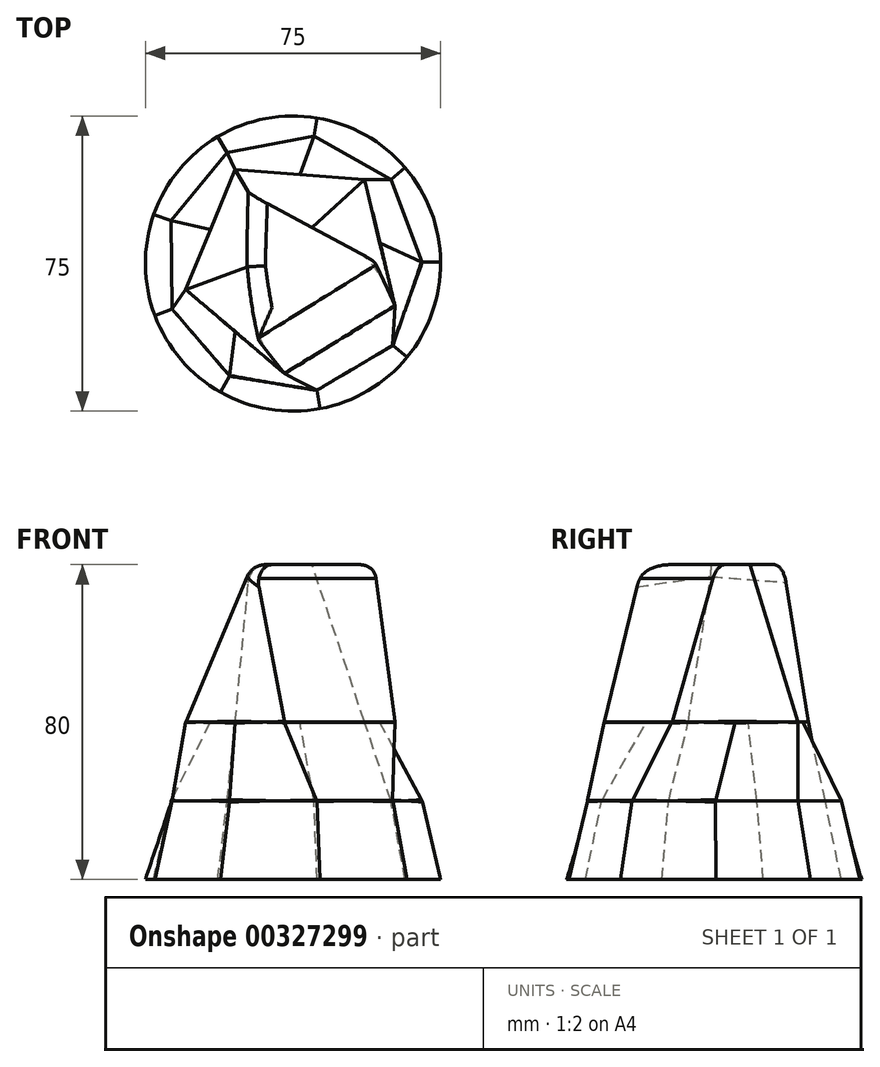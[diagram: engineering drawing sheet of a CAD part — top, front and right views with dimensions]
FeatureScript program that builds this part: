
annotation { "Feature Type Name" : "Feature", "Feature Type Description" : "" }
export const myFeature = defineFeature(function(context is Context, id is Id, definition is map)
    precondition{}
    {
        {
            var Q0;
            Q0=qCreatedBy(makeId("Top.planeOp"),FACE);
            var sketch = newSketch(context, id + "F0", { "sketchPlane" : qUnion([Q0])});
            skCircle(sketch, "E0", {"center": v(0, 0) * mm, "radius": 37.5 * mm});
            skSolve(sketch);
        }
        {
            var Q0;
            Q0=qCreatedBy(makeId("Top.planeOp"),FACE);
            cPlane(context, id + "F1", {"entities" : qUnion([Q0]), "cplaneType" : CPlaneType.OFFSET, "offset" : 20 * mm, "width" : 150 * mm, "height" : 150 * mm});
        }
        {
            var Q0;
            Q0=qCreatedBy(id+"F1.planeOp",FACE);
            var sketch = newSketch(context, id + "F2", { "sketchPlane" : qUnion([Q0])});
            skLineSegment(sketch, "E1.0", {"start": v(-16.7, 28.2) * mm, "end": v(5.34, 32.34) * mm});
            skLineSegment(sketch, "E1.1", {"start": v(5.34, 32.34) * mm, "end": v(24.88, 21.34) * mm});
            skLineSegment(sketch, "E1.2", {"start": v(24.88, 21.34) * mm, "end": v(32.77, 0.35) * mm});
            skLineSegment(sketch, "E1.3", {"start": v(32.77, 0.35) * mm, "end": v(25.33, -20.8) * mm});
            skLineSegment(sketch, "E1.4", {"start": v(25.33, -20.8) * mm, "end": v(6.04, -32.21) * mm});
            skLineSegment(sketch, "E1.5", {"start": v(6.04, -32.21) * mm, "end": v(-16.08, -28.56) * mm});
            skLineSegment(sketch, "E1.6", {"start": v(-16.08, -28.56) * mm, "end": v(-30.68, -11.54) * mm});
            skLineSegment(sketch, "E1.7", {"start": v(-30.68, -11.54) * mm, "end": v(-30.92, 10.88) * mm});
            skLineSegment(sketch, "E1.8", {"start": v(-30.92, 10.88) * mm, "end": v(-16.7, 28.2) * mm});
            skSolve(sketch);
        }
        {
            var Q0;
            Q0=qCreatedBy(id+"F1.planeOp",FACE);
            cPlane(context, id + "F3", {"entities" : qUnion([Q0]), "cplaneType" : CPlaneType.OFFSET, "offset" : 20 * mm, "width" : 150 * mm, "height" : 150 * mm});
        }
        {
            var Q0;
            Q0=qCreatedBy(id+"F3.planeOp",FACE);
            var sketch = newSketch(context, id + "F4", { "sketchPlane" : qUnion([Q0])});
            skLineSegment(sketch, "E2.0", {"start": v(-14.68, 23.89) * mm, "end": v(18.18, 21.34) * mm});
            skLineSegment(sketch, "E2.1", {"start": v(18.18, 21.34) * mm, "end": v(25.92, -10.7) * mm});
            skLineSegment(sketch, "E2.2", {"start": v(25.92, -10.7) * mm, "end": v(-2.17, -27.95) * mm});
            skLineSegment(sketch, "E2.3", {"start": v(-2.17, -27.95) * mm, "end": v(-27.25, -6.58) * mm});
            skLineSegment(sketch, "E2.4", {"start": v(-27.25, -6.58) * mm, "end": v(-14.68, 23.89) * mm});
            skSolve(sketch);
        }
        {
            var Q0;
            Q0=qCreatedBy(id+"F3.planeOp",FACE);
            cPlane(context, id + "F5", {"entities" : qUnion([Q0]), "cplaneType" : CPlaneType.OFFSET, "offset" : 20 * mm, "width" : 150 * mm, "height" : 150 * mm});
        }
        {
            var Q0;
            Q0=qCreatedBy(id+"F5.planeOp",FACE);
            cPlane(context, id + "F6", {"entities" : qUnion([Q0]), "cplaneType" : CPlaneType.OFFSET, "offset" : 20 * mm, "width" : 150 * mm, "height" : 150 * mm});
        }
        {
            var Q0;
            Q0=qCreatedBy(id+"F6.planeOp",FACE);
            var sketch = newSketch(context, id + "F7", { "sketchPlane" : qUnion([Q0])});
            skLineSegment(sketch, "E3.0", {"start": v(-10.94, 17.56) * mm, "end": v(20.67, 0.7) * mm});
            skLineSegment(sketch, "E3.1", {"start": v(20.67, 0.7) * mm, "end": v(-9.74, -18.25) * mm});
            skLineSegment(sketch, "E3.2", {"start": v(-9.74, -18.25) * mm, "end": v(-10.94, 17.56) * mm});
            skSolve(sketch);
        }
        {
            var Q0;
            Q0 = qSketchRegion(id + "F0", true);
            var Q1;
            Q1 = qSketchRegion(id + "F2", true);
            loft(context, id + "F8", {"sheetProfilesArray" : [{ "sheetProfileEntities" : qUnion([Q0]) }, { "sheetProfileEntities" : qUnion([Q1]) }]});
        }
        {
            var Q1;
            Q1 = qSketchRegion(id + "F2", true);
            var Q2;
            Q2 = qSketchRegion(id + "F4", true);
            loft(context, id + "F9", {"operationType" : NewBodyOperationType.ADD, "sheetProfilesArray" : [{ "sheetProfileEntities" : qUnion([Q1]) }, { "sheetProfileEntities" : qUnion([Q2]) }]});
        }
        {
            var Q1;
            Q1 = qSketchRegion(id + "F4", true);
            var Q2;
            Q2 = qSketchRegion(id + "F7", true);
            loft(context, id + "F10", {"operationType" : NewBodyOperationType.ADD, "sheetProfilesArray" : [{ "sheetProfileEntities" : qUnion([Q1]) }, { "sheetProfileEntities" : qUnion([Q2]) }]});
        }
        {
            var Q0;
            {var subQ0=sQuery(id+"F7.wireOp",EDGE,"E3.1");var subQ1=sQuery(id+"F7.wireOp",EDGE,"E3.2");var subQ2=sQuery(id+"F7.wireOp",EDGE,"E3.0");Q0=makeQuery(id+"F10.opLoft","MID_CAP_EDGE",EDGE,{"disambiguationData":[OSD([subQ2,subQ0,subQ1]),TDD([makeQuery(id+"F7.imprint","INTERSECT",VERTEX,{"derivedFrom":[subQ2,subQ0]}),makeQuery(id+"F7.imprint","INTERSECT",VERTEX,{"derivedFrom":[subQ0,subQ1]}),makeQuery(id+"F7.imprint","IMPRINT",EDGE,{"derivedFrom":subQ0})])],"capPos":1.0});}
            var Q1;
            {var subQ0=sQuery(id+"F7.wireOp",EDGE,"E3.0");var subQ1=sQuery(id+"F7.wireOp",EDGE,"E3.1");var subQ2=sQuery(id+"F7.wireOp",EDGE,"E3.2");Q1=makeQuery(id+"F10.opLoft","MID_CAP_EDGE",EDGE,{"disambiguationData":[OSD([subQ0,subQ1,subQ2]),TDD([makeQuery(id+"F7.imprint","INTERSECT",VERTEX,{"derivedFrom":[subQ0,subQ2]}),makeQuery(id+"F7.imprint","INTERSECT",VERTEX,{"derivedFrom":[subQ0,subQ1]}),makeQuery(id+"F7.imprint","IMPRINT",EDGE,{"derivedFrom":subQ0})])],"capPos":1.0});}
            var Q2;
            Q2=makeQuery(id+"F10.opLoft","MID_CAP_EDGE",EDGE,{"disambiguationData":[OSD([sQuery(id+"F4.wireOp",EDGE,"E2.0"),sQuery(id+"F4.wireOp",EDGE,"E2.3"),sQuery(id+"F4.wireOp",EDGE,"E2.4"),sQuery(id+"F7.wireOp",EDGE,"E3.2")])],"capPos":1.0});
            var Q3;
            Q3=makeQuery(id+"F10.opLoft","MID_CAP_EDGE",EDGE,{"disambiguationData":[OSD([sQuery(id+"F4.wireOp",EDGE,"E2.0"),sQuery(id+"F4.wireOp",EDGE,"E2.4"),sQuery(id+"F7.wireOp",EDGE,"E3.0"),sQuery(id+"F7.wireOp",EDGE,"E3.2")])],"capPos":1.0});
            var Q4;
            Q4=makeQuery(id+"F10.opLoft","MID_CAP_EDGE",EDGE,{"disambiguationData":[OSD([sQuery(id+"F4.wireOp",EDGE,"E2.3"),sQuery(id+"F4.wireOp",EDGE,"E2.4"),sQuery(id+"F7.wireOp",EDGE,"E3.1"),sQuery(id+"F7.wireOp",EDGE,"E3.2")])],"capPos":1.0});
            fillet(context, id + "F11", {"entities" : qUnion([Q0, Q1, Q2, Q3, Q4]), "radius" : 5 * mm, "tangentPropagation" : true, "allowEdgeOverflow" : false});
        }
        {
            var Q0;
            {var subQ0=sQuery(id+"F4.wireOp",EDGE,"E2.4");var subQ1=sQuery(id+"F4.wireOp",EDGE,"E2.3");var subQ2=sQuery(id+"F4.wireOp",EDGE,"E2.2");Q0=makeQuery(id+"F10.boolean.opBoolean","MERGE",EDGE,{"derivedFrom":[makeQuery(id+"F9.opLoft","MID_CAP_EDGE",EDGE,{"disambiguationData":[OSD([subQ2,subQ1,subQ0])],"capPos":1.0}),makeQuery(id+"F10.opLoft","MID_CAP_EDGE",EDGE,{"disambiguationData":[OSD([subQ2,subQ1,subQ0])],"capPos":0.0})]});}
            var Q1;
            {var subQ0=sQuery(id+"F4.wireOp",EDGE,"E2.3");var subQ1=sQuery(id+"F4.wireOp",EDGE,"E2.2");var subQ2=sQuery(id+"F4.wireOp",EDGE,"E2.1");Q1=makeQuery(id+"F10.boolean.opBoolean","MERGE",EDGE,{"derivedFrom":[makeQuery(id+"F9.opLoft","MID_CAP_EDGE",EDGE,{"disambiguationData":[OSD([subQ2,subQ1,subQ0])],"capPos":1.0}),makeQuery(id+"F10.opLoft","MID_CAP_EDGE",EDGE,{"disambiguationData":[OSD([subQ2,subQ1,subQ0])],"capPos":0.0})]});}
            var Q2;
            {var subQ0=sQuery(id+"F4.wireOp",EDGE,"E2.2");var subQ1=sQuery(id+"F4.wireOp",EDGE,"E2.1");var subQ2=sQuery(id+"F4.wireOp",EDGE,"E2.0");Q2=makeQuery(id+"F10.boolean.opBoolean","MERGE",EDGE,{"derivedFrom":[makeQuery(id+"F9.opLoft","MID_CAP_EDGE",EDGE,{"disambiguationData":[OSD([subQ2,subQ1,subQ0])],"capPos":1.0}),makeQuery(id+"F10.opLoft","MID_CAP_EDGE",EDGE,{"disambiguationData":[OSD([subQ2,subQ1,subQ0])],"capPos":0.0})]});}
            var Q3;
            {var subQ0=sQuery(id+"F2.wireOp",EDGE,"E1.4");var subQ1=sQuery(id+"F2.wireOp",EDGE,"E1.3");var subQ2=sQuery(id+"F2.wireOp",EDGE,"E1.2");Q3=makeQuery(id+"F9.boolean.opBoolean","MERGE",EDGE,{"derivedFrom":[makeQuery(id+"F8.opLoft","MID_CAP_EDGE",EDGE,{"disambiguationData":[OSD([subQ2,subQ1,subQ0])],"capPos":1.0}),makeQuery(id+"F9.opLoft","MID_CAP_EDGE",EDGE,{"disambiguationData":[OSD([subQ2,subQ1,subQ0])],"capPos":0.0})]});}
            var Q4;
            {var subQ0=sQuery(id+"F2.wireOp",EDGE,"E1.5");var subQ1=sQuery(id+"F2.wireOp",EDGE,"E1.4");var subQ2=sQuery(id+"F2.wireOp",EDGE,"E1.3");Q4=makeQuery(id+"F9.boolean.opBoolean","MERGE",EDGE,{"derivedFrom":[makeQuery(id+"F8.opLoft","MID_CAP_EDGE",EDGE,{"disambiguationData":[OSD([subQ2,subQ1,subQ0])],"capPos":1.0}),makeQuery(id+"F9.opLoft","MID_CAP_EDGE",EDGE,{"disambiguationData":[OSD([subQ2,subQ1,subQ0])],"capPos":0.0})]});}
            var Q5;
            {var subQ0=sQuery(id+"F2.wireOp",EDGE,"E1.6");var subQ1=sQuery(id+"F2.wireOp",EDGE,"E1.5");var subQ2=sQuery(id+"F2.wireOp",EDGE,"E1.4");Q5=makeQuery(id+"F9.boolean.opBoolean","MERGE",EDGE,{"derivedFrom":[makeQuery(id+"F8.opLoft","MID_CAP_EDGE",EDGE,{"disambiguationData":[OSD([subQ2,subQ1,subQ0])],"capPos":1.0}),makeQuery(id+"F9.opLoft","MID_CAP_EDGE",EDGE,{"disambiguationData":[OSD([subQ2,subQ1,subQ0])],"capPos":0.0})]});}
            var Q6;
            {var subQ0=sQuery(id+"F2.wireOp",EDGE,"E1.7");var subQ1=sQuery(id+"F2.wireOp",EDGE,"E1.6");var subQ2=sQuery(id+"F2.wireOp",EDGE,"E1.5");Q6=makeQuery(id+"F9.boolean.opBoolean","MERGE",EDGE,{"derivedFrom":[makeQuery(id+"F8.opLoft","MID_CAP_EDGE",EDGE,{"disambiguationData":[OSD([subQ2,subQ1,subQ0])],"capPos":1.0}),makeQuery(id+"F9.opLoft","MID_CAP_EDGE",EDGE,{"disambiguationData":[OSD([subQ2,subQ1,subQ0])],"capPos":0.0})]});}
            fillet(context, id + "F12", {"entities" : qUnion([Q0, Q1, Q2, Q3, Q4, Q5, Q6]), "radius" : 2 * mm, "tangentPropagation" : true, "allowEdgeOverflow" : false});
        }
    });
